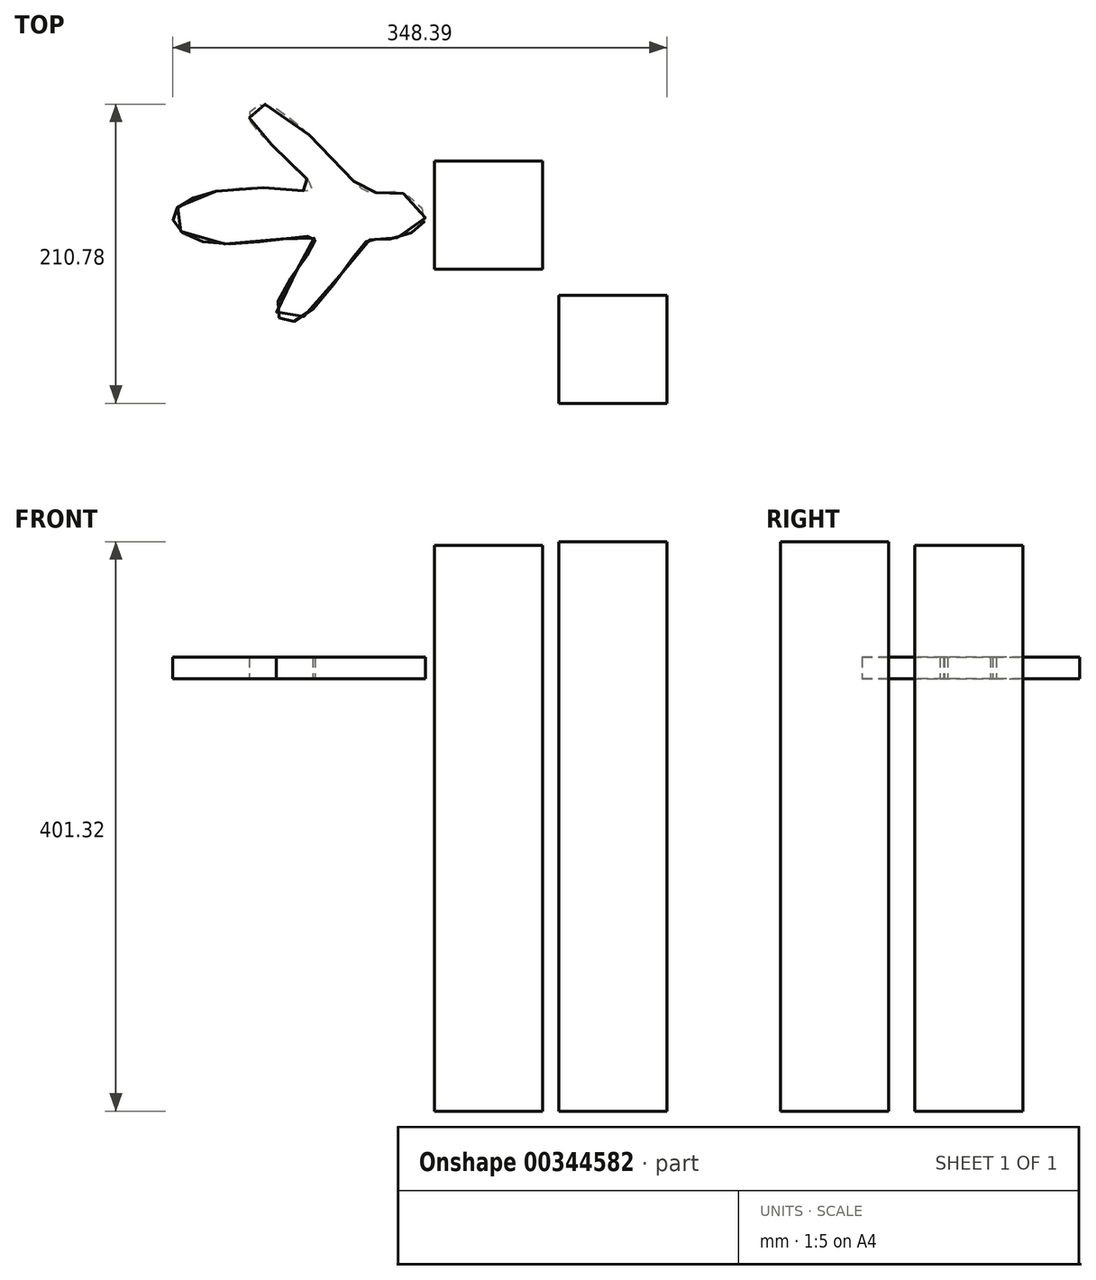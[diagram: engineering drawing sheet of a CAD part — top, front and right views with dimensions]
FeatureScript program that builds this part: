
annotation { "Feature Type Name" : "Feature", "Feature Type Description" : "" }
export const myFeature = defineFeature(function(context is Context, id is Id, definition is map)
    precondition{}
    {
        {
            var Q0;
            Q0=qCreatedBy(makeId("Top.planeOp"),FACE);
            var sketch = newSketch(context, id + "F0", { "sketchPlane" : qUnion([Q0])});
            skLineSegment(sketch, "E0.bottom", {"start": v(0, 3.12) * mm, "end": v(-76.2, 3.12) * mm});
            skLineSegment(sketch, "E0.top", {"start": v(0, 79.32) * mm, "end": v(-76.2, 79.32) * mm});
            skLineSegment(sketch, "E0.left", {"start": v(0, 3.12) * mm, "end": v(0, 79.32) * mm});
            skLineSegment(sketch, "E0.right", {"start": v(-76.2, 3.12) * mm, "end": v(-76.2, 79.32) * mm});
            skLineSegment(sketch, "E1.bottom", {"start": v(5.54, 3.12) * mm, "end": v(81.74, 3.12) * mm});
            skLineSegment(sketch, "E1.top", {"start": v(5.54, 79.32) * mm, "end": v(81.74, 79.32) * mm});
            skLineSegment(sketch, "E1.left", {"start": v(5.54, 3.12) * mm, "end": v(5.54, 79.32) * mm});
            skLineSegment(sketch, "E1.right", {"start": v(81.74, 3.12) * mm, "end": v(81.74, 79.32) * mm});
            skSolve(sketch);
        }
        {
            var Q0;
            Q0=makeQuery(id+"F0.imprint","IMPRINT",FACE,{"disambiguationData":[TD([[makeQuery(id+"F0.imprint","IMPRINT",EDGE,{"derivedFrom":sQuery(id+"F0.wireOp",EDGE,"E0.bottom")}),-1.0]])]});
            extrude(context, id + "F1", {"entities" : qUnion([Q0]), "depth" : 398.78 * mm});
        }
        {
            var Q0;
            Q0=qCreatedBy(makeId("Top.planeOp"),FACE);
            var sketch = newSketch(context, id + "F2", { "sketchPlane" : qUnion([Q0])});
            skLineSegment(sketch, "E2.bottom", {"start": v(11.43, -15.2) * mm, "end": v(87.63, -15.2) * mm});
            skLineSegment(sketch, "E2.top", {"start": v(11.43, -91.4) * mm, "end": v(87.63, -91.4) * mm});
            skLineSegment(sketch, "E2.left", {"start": v(11.43, -15.2) * mm, "end": v(11.43, -91.4) * mm});
            skLineSegment(sketch, "E2.right", {"start": v(87.63, -15.2) * mm, "end": v(87.63, -91.4) * mm});
            skSolve(sketch);
        }
        {
            var Q0;
            Q0=makeQuery(id+"F2.imprint","IMPRINT",FACE,{"disambiguationData":[TD([[makeQuery(id+"F2.imprint","IMPRINT",EDGE,{"derivedFrom":sQuery(id+"F2.wireOp",EDGE,"E2.bottom")}),-1.0]])]});
            extrude(context, id + "F3", {"entities" : qUnion([Q0]), "depth" : 401.32 * mm});
        }
        {
            var Q0;
            Q0=qCreatedBy(makeId("Top.planeOp"),FACE);
            cPlane(context, id + "F4", {"entities" : qUnion([Q0]), "cplaneType" : CPlaneType.OFFSET, "offset" : 304.8 * mm, "width" : 152.4 * mm, "height" : 152.4 * mm});
        }
        {
            var Q0;
            Q0=qCreatedBy(id+"F4.planeOp",FACE);
            var sketch = newSketch(context, id + "F5", { "sketchPlane" : qUnion([Q0])});
            skFitSpline(sketch, "E3", {"points": [v(-230.27, 58.12) * mm, v(-176.38, 59.2) * mm, v(-161.9, 59.93) * mm, v(-194.73, 94.16) * mm, v(-206.63, 112.78) * mm, v(-192.83, 118.7) * mm, v(-127.6, 59.97) * mm, v(-117.75, 56.93) * mm, v(-97.93, 56.24) * mm, v(-83.31, 36.47) * mm, v(-115.07, 23.64) * mm, v(-124.33, 22.35) * mm, v(-172.79, -32.8) * mm, v(-187.59, -24.68) * mm, v(-160.41, 22.78) * mm, v(-169.42, 26.02) * mm, v(-240.18, 22.76) * mm, v(-260.63, 41.15) * mm, v(-230.27, 58.12) * mm]});
            skSolve(sketch);
        }
        {
            var Q0;
            Q0=makeQuery(id+"F5.imprint","IMPRINT",FACE,{"disambiguationData":[TD([[makeQuery(id+"F5.imprint","IMPRINT",EDGE,{"derivedFrom":sQuery(id+"F5.wireOp",EDGE,"E3")}),-1.0]])]});
            extrude(context, id + "F6", {"entities" : qUnion([Q0]), "depth" : 15.24 * mm});
        }
    });
